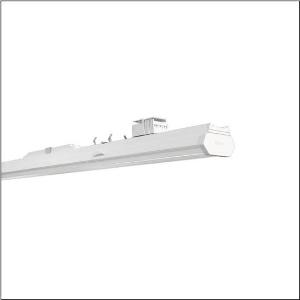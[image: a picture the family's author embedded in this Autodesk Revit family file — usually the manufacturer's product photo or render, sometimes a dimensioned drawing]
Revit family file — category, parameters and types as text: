
# Revit family: licross_r__11_protected_mo_51tp12cn49xg_4f1c
name_source: partatom
category: Lighting Fixtures
units: mm (PartAtom-declared; Revit-internal decimal feet)

## family parameters
Cut with Voids When Loaded = No
Host = Face
Light Source = No
Part Type = Normal
Room Calculation Point = No
Round Connector Dimension = Use Diameter
Shared = No

## types (1)
- --- (1 x LED, 9070 lm, 49.4 W, 4000K)
    Apparent Load = 49 VA
    CIE Flux Codes = 73 92 98 99 100
    Color Rendering = 80
    Color Temperature = 4000K
    Default Elevation = 1800 mm
    Description = Licross® 11 Protected MO, luminaire insert, of sheet steel, galvanised, coil coated, white, length: 1.500mm, width: 90mm, height: 101mm, LED rated luminous flux: 9.070lm, light colour: 840, control gear: ON/OFF Multilumen, CLOi, with plug, 3-pole, with phase selection, mains connection: 220..240V, AC, 50/60Hz, start of lifetime: 49W, end of service life: 55W, halogen-free wiring, primary light control with lens, of plastic, primary optical cover: cover, of PMMA, light emission: direct distribution, primary light characteristic: symmetric, protection rating (complete): IP64, insulation class (complete): insulation class I (protective earthing), certification: CE, ENEC, VDE, UKCA, protection symbol: D if used in an environment with conductive dust loads with corresponding accessories, impact resistance: IK06, permissible ambient temperature for indoor applications: -35..+40°C, corresponds to IFS (International Featured Standards) requirements for safety and quality in the food industry, reducing of maximum allowable ambient temperature of 5°C with ceiling mounting, LABS conformity tested according to VDMA 24364:2018-05, packaging unit: 1 piece
    Height = 92 mm
    Lamp = 1 x LED
    Lamp Light Flux = 9070 lm
    Lamp Power = 49.4 W
    Lamp count = 1
    Length = 1500 mm
    Luminous efficacy = 184 lm/W
    Manufacturer = Siteco
    ModVariant = No
    Model = 51TP12CN49XG
    Mounting Place = Ceiling
    Mounting Type = Pendant
    Number of Poles = 1
    OnlyDefault = Yes
    Power Factor = 1
    Product Name = Licross® 11 Protected MO
    Product group = luminaire insert
    ProductGroupID = 901
    Protection Class = Protection class I
    Protection Degree = IP 64
    RLX_Detail_Level = 1
    RLX_Emergency_Light_Flux = 0 lm
    RLX_Emergency_Type = 0
    RLX_Emergency_Type_DB = No
    RlxData = <blob elided: 22037 chars, md5=29933d19>
    Socket = socket
    Standby Power = 0 W
    System Light Flux = 9070 lm
    System Power = 49 W
    Type Comments = factory setting: luminous flux: 100 % | (A | C | E) | 113 mA
    Type Image = l_1256148.jpg
    URL = http://relux.com
    VarID = @adj_038073
    Voltage = 0 V
    Weight = 0.00 kg
    Width = 88 mm

## geometry (parser evidence)
native form markers: Blend x4, Sweep x9
no freeform markers — native parametric forms only
